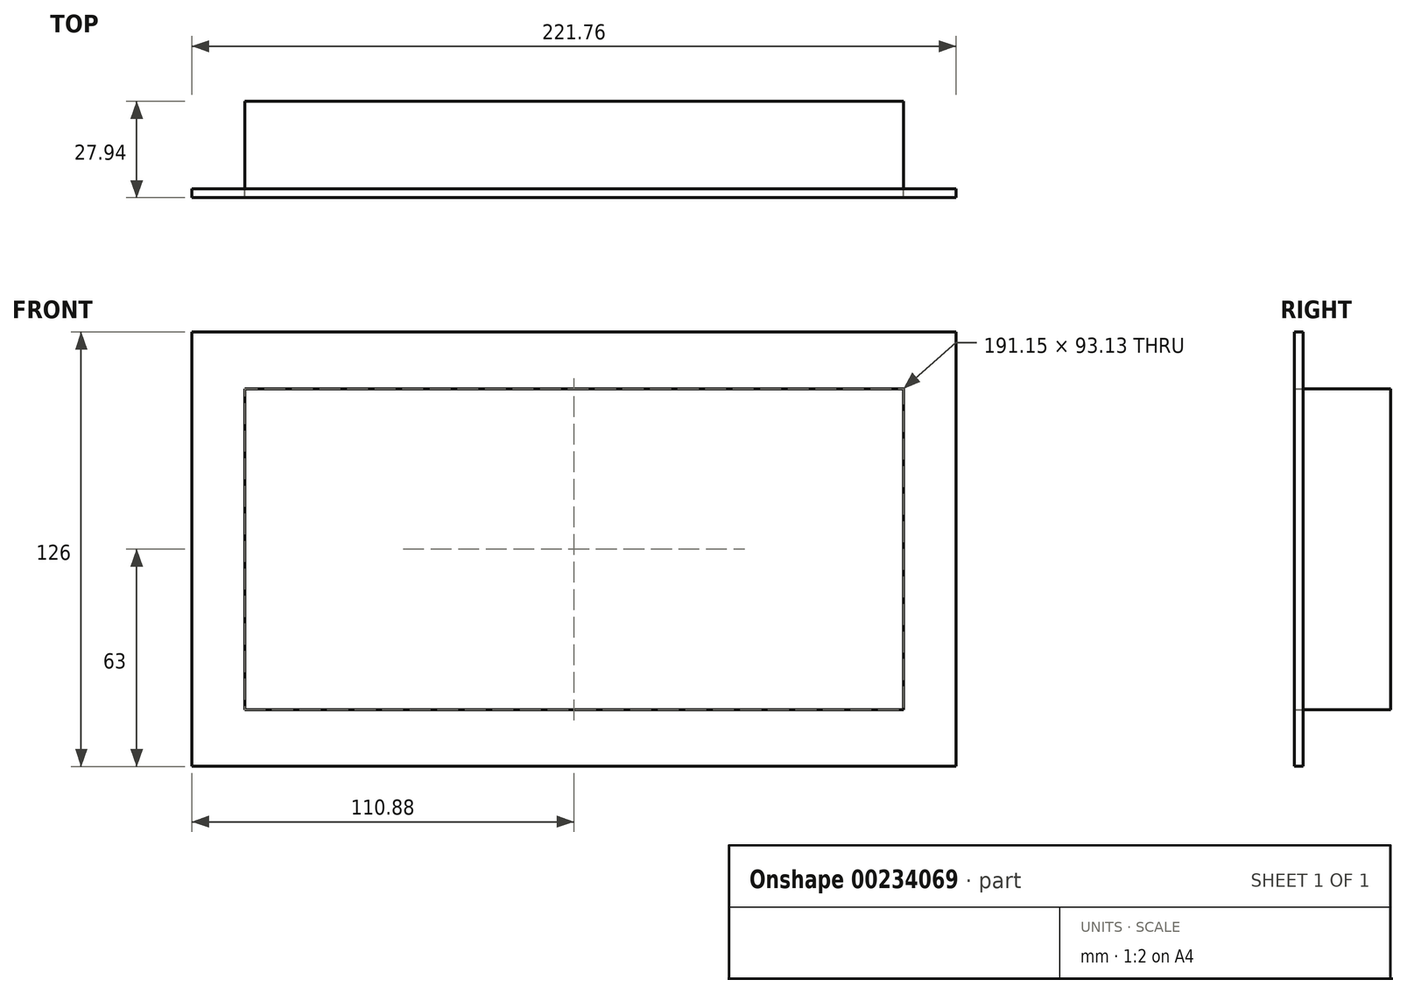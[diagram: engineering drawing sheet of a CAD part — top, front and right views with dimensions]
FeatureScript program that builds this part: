
annotation { "Feature Type Name" : "Feature", "Feature Type Description" : "" }
export const myFeature = defineFeature(function(context is Context, id is Id, definition is map)
    precondition{}
    {
        {
            var Q0;
            Q0=qCreatedBy(makeId("Front.planeOp"),FACE);
            var sketch = newSketch(context, id + "F3", { "sketchPlane" : qUnion([Q0])});
            skLineSegment(sketch, "E0.bottom", {"start": v(95.58, -46.56) * mm, "end": v(-95.58, -46.56) * mm});
            skLineSegment(sketch, "E0.top", {"start": v(95.58, 46.56) * mm, "end": v(-95.58, 46.56) * mm});
            skLineSegment(sketch, "E0.left", {"start": v(95.58, -46.56) * mm, "end": v(95.58, 46.56) * mm});
            skLineSegment(sketch, "E0.right", {"start": v(-95.58, -46.56) * mm, "end": v(-95.58, 46.56) * mm});
            skPoint(sketch, "E0.middle", {"position": v(0, 0) * mm});
            skLineSegment(sketch, "E1.bottom", {"start": v(110.88, -63) * mm, "end": v(-110.88, -63) * mm});
            skLineSegment(sketch, "E1.top", {"start": v(110.88, 63) * mm, "end": v(-110.88, 63) * mm});
            skLineSegment(sketch, "E1.left", {"start": v(110.88, -63) * mm, "end": v(110.88, 63) * mm});
            skLineSegment(sketch, "E1.right", {"start": v(-110.88, -63) * mm, "end": v(-110.88, 63) * mm});
            skSolve(sketch);
        }
        {
            var Q0;
            Q0=makeQuery(id+"F3.imprint","IMPRINT",FACE,{"disambiguationData":[TD([[makeQuery(id+"F3.imprint","IMPRINT",EDGE,{"derivedFrom":sQuery(id+"F3.wireOp",EDGE,"E0.bottom")}),-1.0]])]});
            extrude(context, id + "F0", {"entities" : qUnion([Q0]), "oppositeDirection" : true, "depth" : 25.4 * mm});
        }
        {
            var Q0;
            Q0=makeQuery(id+"F3.imprint","IMPRINT",FACE,{"disambiguationData":[TD([[makeQuery(id+"F3.imprint","IMPRINT",EDGE,{"derivedFrom":sQuery(id+"F3.wireOp",EDGE,"E0.bottom")}),1.0]])]});
            extrude(context, id + "F1", {"entities" : qUnion([Q0]), "depth" : 2.54 * mm});
        }
        {
            var Q0;
            Q0=makeQuery(id+"F1.opExtrude","CAP_FACE",FACE,{"disambiguationData":[OSD([sQuery(id+"F3.wireOp",EDGE,"E0.bottom"),sQuery(id+"F3.wireOp",EDGE,"E0.top"),sQuery(id+"F3.wireOp",EDGE,"E0.left"),sQuery(id+"F3.wireOp",EDGE,"E0.right"),sQuery(id+"F3.wireOp",EDGE,"E1.bottom"),sQuery(id+"F3.wireOp",EDGE,"E1.top"),sQuery(id+"F3.wireOp",EDGE,"E1.left"),sQuery(id+"F3.wireOp",EDGE,"E1.right")])],"isStart":false});
            shell(context, id + "F2", {"entities" : qUnion([Q0]), "thickness" : 2.54 * mm});
        }
    });
